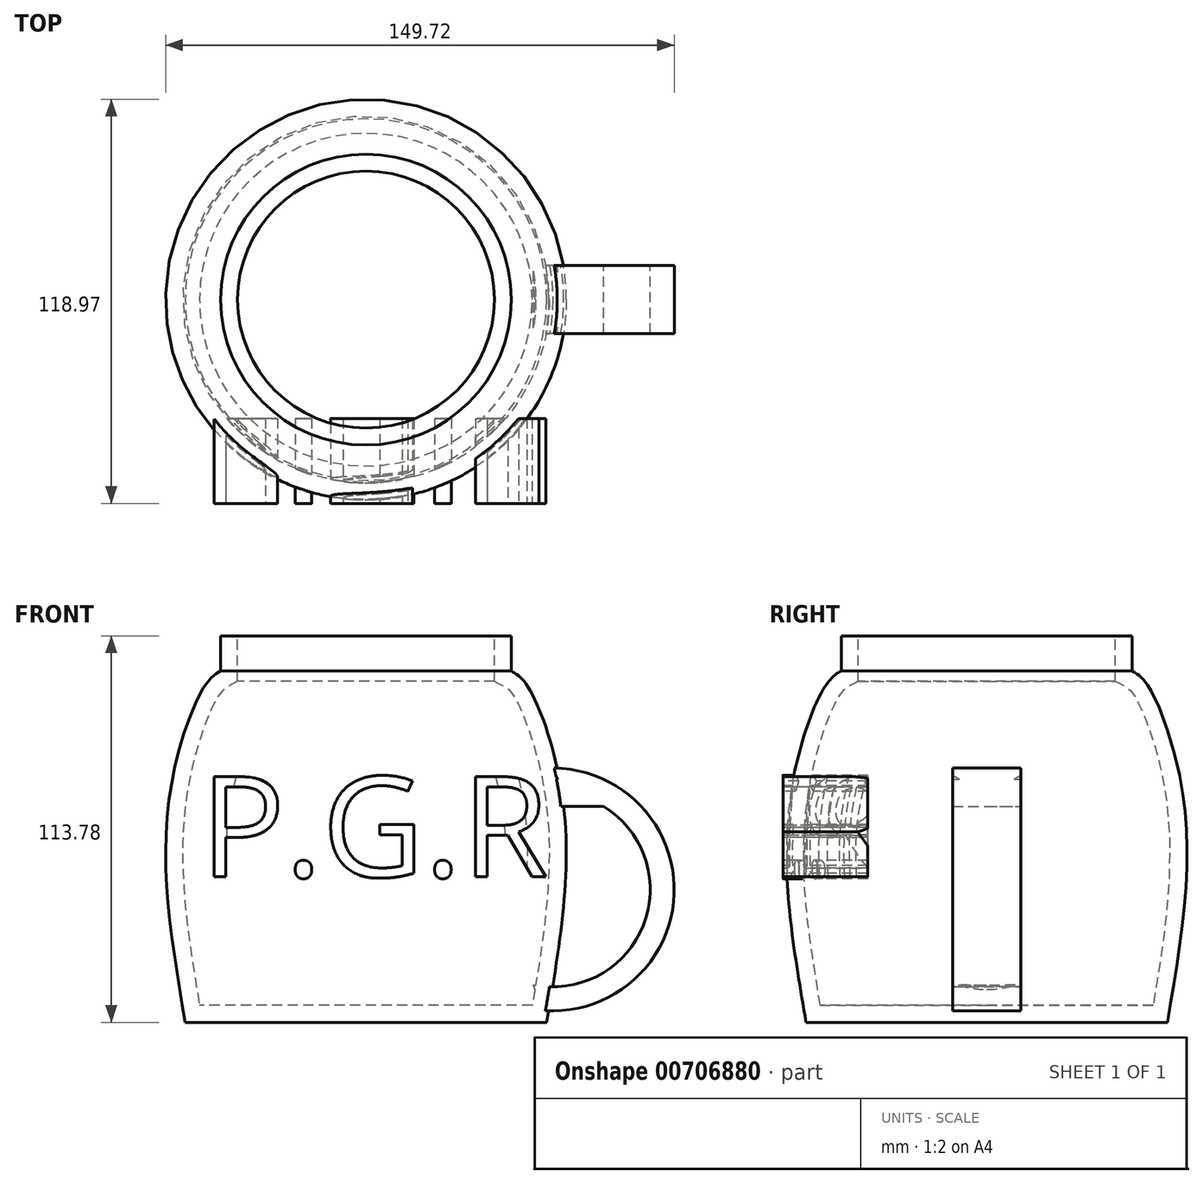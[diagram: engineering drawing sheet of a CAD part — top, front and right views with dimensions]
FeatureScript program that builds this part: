
annotation { "Feature Type Name" : "Feature", "Feature Type Description" : "" }
export const myFeature = defineFeature(function(context is Context, id is Id, definition is map)
    precondition{}
    {
        {
            var Q0;
            Q0=qCreatedBy(makeId("Front.planeOp"),FACE);
            var sketch = newSketch(context, id + "F0", { "sketchPlane" : qUnion([Q0])});
            skLineSegment(sketch, "E0", {"start": v(0, 50.22) * mm, "end": v(0, -63.56) * mm});
            skLineSegment(sketch, "E1", {"start": v(0, -63.56) * mm, "end": v(-53.19, -63.56) * mm});
            skLineSegment(sketch, "E2", {"start": v(0, 50.22) * mm, "end": v(-42.82, 50.22) * mm});
            skFitSpline(sketch, "E3", {"points": [v(-42.82, 50.22) * mm, v(-42.82, 39.85) * mm], "startDerivative": vector(0, -10.37) * mm, "endDerivative": vector(0, -10.37) * mm});
            skFitSpline(sketch, "E4", {"points": [v(-42.82, 39.85) * mm, v(-46.97, 36.3) * mm, v(-58.22, 0) * mm, v(-53.19, -63.56) * mm], "startDerivative": vector(-27.82, -15.45) * mm, "endDerivative": vector(22.9, -133.7) * mm});
            skSolve(sketch);
        }
        {
            var Q0;
            Q0=makeQuery(id+"F0.imprint","IMPRINT",FACE,{"disambiguationData":[TD([[makeQuery(id+"F0.imprint","IMPRINT",EDGE,{"derivedFrom":sQuery(id+"F0.wireOp",EDGE,"E0")}),-1.0]])]});
            var Q1;
            Q1=sQuery(id+"F0.wireOp",EDGE,"E0");
            revolve(context, id + "F1", {"surfaceOperationType" : NewSurfaceOperationType.NEW, "entities" : qUnion([Q0]), "axis" : qUnion([Q1]), "revolveType" : RevolveType.FULL});
        }
        {
            var Q0;
            Q0=makeQuery(id+"F1.opRevolve","SWEPT_FACE",FACE,{"disambiguationData":[OSD([sQuery(id+"F0.wireOp",EDGE,"E2")])]});
            shell(context, id + "F2", {"entities" : qUnion([Q0]), "thickness" : 5 * mm});
        }
        {
            var Q0;
            Q0=qCreatedBy(makeId("Right.planeOp"),FACE);
            cPlane(context, id + "F3", {"entities" : qUnion([Q0]), "cplaneType" : CPlaneType.OFFSET, "offset" : 55 * mm, "width" : 150 * mm, "height" : 150 * mm});
        }
        {
            var Q0;
            Q0=qCreatedBy(id+"F3.planeOp",FACE);
            var sketch = newSketch(context, id + "F4", { "sketchPlane" : qUnion([Q0])});
            skLineSegment(sketch, "E5.bottom", {"start": v(-10, 0) * mm, "end": v(10, 0) * mm});
            skLineSegment(sketch, "E5.top", {"start": v(-10, 8) * mm, "end": v(10, 8) * mm});
            skLineSegment(sketch, "E5.left", {"start": v(-10, 0) * mm, "end": v(-10, 8) * mm});
            skLineSegment(sketch, "E5.right", {"start": v(10, 0) * mm, "end": v(10, 8) * mm});
            skSolve(sketch);
        }
        {
            var Q0;
            Q0 = qSketchRegion(id + "F4", true);
            extrude(context, id + "F5", {"entities" : qUnion([Q0]), "operationType" : NewBodyOperationType.ADD, "depth" : 15 * mm, "offsetDistance" : 25 * mm});
        }
        {
            var Q0;
            Q0=qCreatedBy(id+"F3.planeOp",FACE);
            var sketch = newSketch(context, id + "F6", { "sketchPlane" : qUnion([Q0])});
            skLineSegment(sketch, "E6", {"start": v(0, -24.45) * mm, "end": v(-13.19, -24.45) * mm});
            skSolve(sketch);
        }
        {
            var Q0;
            Q0=makeQuery(id+"F5.opExtrude","CAP_FACE",FACE,{"disambiguationData":[OSD([sQuery(id+"F4.wireOp",EDGE,"E5.bottom"),sQuery(id+"F4.wireOp",EDGE,"E5.top"),sQuery(id+"F4.wireOp",EDGE,"E5.left"),sQuery(id+"F4.wireOp",EDGE,"E5.right")])],"isStart":false});
            var Q1;
            Q1=sQuery(id+"F6.wireOp",EDGE,"E6");
            revolve(context, id + "F7", {"operationType" : NewBodyOperationType.ADD, "surfaceOperationType" : NewSurfaceOperationType.NEW, "entities" : qUnion([Q0]), "axis" : qUnion([Q1]), "revolveType" : RevolveType.TWO_DIRECTIONS, "angle" : 25 * degree, "angleBack" : 200 * degree});
        }
        {
            var Q0;
            Q0=qCreatedBy(makeId("Front.planeOp"),FACE);
            cPlane(context, id + "F8", {"entities" : qUnion([Q0]), "cplaneType" : CPlaneType.OFFSET, "offset" : 60 * mm, "width" : 150 * mm, "height" : 150 * mm});
        }
        {
            var Q0;
            Q0=qCreatedBy(id+"F8.planeOp",FACE);
            var sketch = newSketch(context, id + "F9", { "sketchPlane" : qUnion([Q0])});
            skText(sketch, "E7", { "text": "P.G.R", "fontName": "OpenSans-Regular.ttf"});
            const initialGuessF9  = {"E7": [-0.04874, -0.02072, 1, 0, 0.02973]};
            skSetInitialGuess(sketch, initialGuessF9);
            skSolve(sketch);
        }
        {
            var Q0;
            Q0 = qSketchRegion(id + "F9", true);
            extrude(context, id + "F10", {"entities" : qUnion([Q0]), "operationType" : NewBodyOperationType.ADD, "oppositeDirection" : true, "depth" : 25 * mm, "offsetDistance" : 25 * mm});
        }
    });
